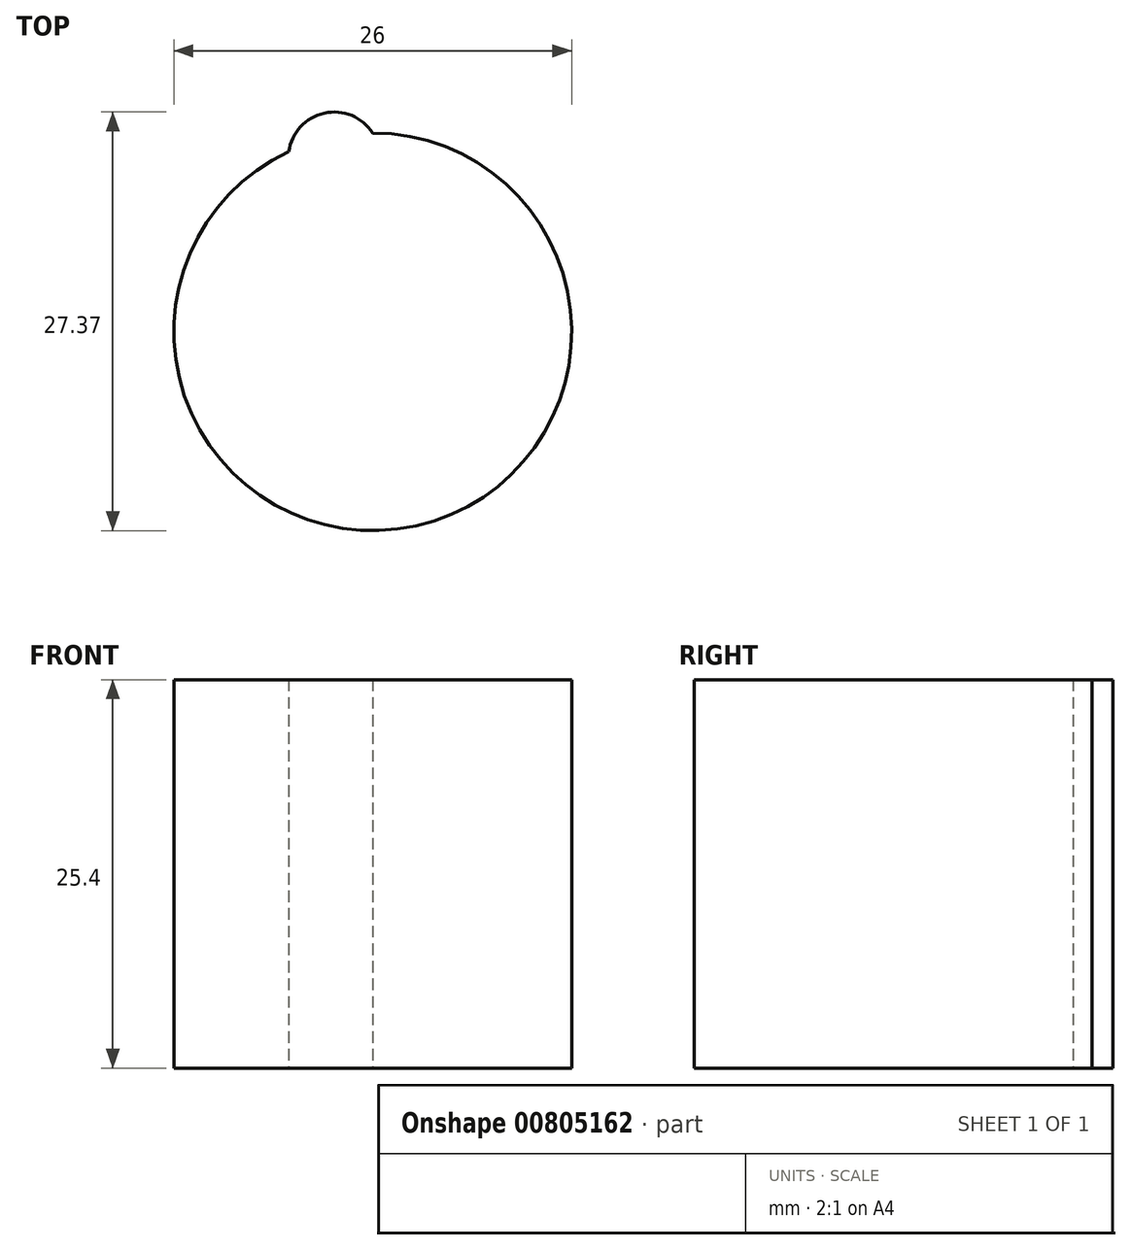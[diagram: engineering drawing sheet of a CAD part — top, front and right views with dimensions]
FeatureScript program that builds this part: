
annotation { "Feature Type Name" : "Feature", "Feature Type Description" : "" }
export const myFeature = defineFeature(function(context is Context, id is Id, definition is map)
    precondition{}
    {
        {
            var Q0;
            Q0=qCreatedBy(makeId("Top.planeOp"),FACE);
            var sketch = newSketch(context, id + "F0", { "sketchPlane" : qUnion([Q0])});
            skCircle(sketch, "E0", {"center": v(0, 0) * mm, "radius": 13 * mm});
            skArc(sketch, "E1", {"start": v(0, 13) * mm, "mid": v(-3.17, 14.3) * mm, "end": v(-5.5, 11.78) * mm});
            skArc(sketch, "E2.1.0", {"start": v(-5.66, 11.7) * mm, "mid": v(-9.08, 11.5) * mm, "end": v(-10.08, 8.22) * mm});
            skArc(sketch, "E2.2.0", {"start": v(-10.2, 8.07) * mm, "mid": v(-13.19, 6.4) * mm, "end": v(-12.67, 3.02) * mm});
            skArc(sketch, "E2.3.0", {"start": v(-12.7, 2.83) * mm, "mid": v(-14.68, 0.03) * mm, "end": v(-12.74, -2.8) * mm});
            skArc(sketch, "E2.4.0", {"start": v(-12.7, -2.98) * mm, "mid": v(-13.26, -6.36) * mm, "end": v(-10.3, -8.06) * mm});
            skArc(sketch, "E2.5.0", {"start": v(-10.17, -8.21) * mm, "mid": v(-9.2, -11.5) * mm, "end": v(-5.8, -11.74) * mm});
            skArc(sketch, "E2.6.0", {"start": v(-5.62, -11.82) * mm, "mid": v(-3.33, -14.37) * mm, "end": v(-0.15, -13.11) * mm});
            skArc(sketch, "E2.7.0", {"start": v(0.05, -13.1) * mm, "mid": v(3.21, -14.4) * mm, "end": v(5.54, -11.9) * mm});
            skArc(sketch, "E2.8.0", {"start": v(5.7, -11.8) * mm, "mid": v(9.13, -11.6) * mm, "end": v(10.13, -8.33) * mm});
            skArc(sketch, "E2.9.0", {"start": v(10.24, -8.17) * mm, "mid": v(13.23, -6.5) * mm, "end": v(12.72, -3.12) * mm});
            skArc(sketch, "E2.10.0", {"start": v(12.75, -2.94) * mm, "mid": v(14.73, -0.14) * mm, "end": v(12.8, 2.69) * mm});
            skArc(sketch, "E2.11.0", {"start": v(12.74, 2.87) * mm, "mid": v(13.3, 6.25) * mm, "end": v(10.34, 7.96) * mm});
            skPoint(sketch, "E2.center", {"position": v(0.02, -0.05) * mm});
            skArc(sketch, "E3.2.12.0", {"start": v(10.21, 8.1) * mm, "mid": v(9.26, 11.4) * mm, "end": v(5.84, 11.64) * mm});
            skArc(sketch, "E3.2.13.0", {"start": v(5.67, 11.72) * mm, "mid": v(3.38, 14.26) * mm, "end": v(0.2, 13) * mm});
            skSolve(sketch);
        }
        {
            var Q0;
            {var subQ0=sQuery(id+"F0.wireOp",EDGE,"E1");var subQ1=sQuery(id+"F0.wireOp",EDGE,"E0");var subQ2=makeQuery(id+"F0.imprint","INTERSECT",VERTEX,{"disambiguationData":[OD(0.0)],"derivedFrom":[subQ1,subQ0]});Q0=makeQuery(id+"F0.imprint","IMPRINT",FACE,{"disambiguationData":[TD([[makeQuery(id+"F0.imprint","IMPRINT",EDGE,{"disambiguationData":[TD([[subQ2,-1.0]])],"derivedFrom":subQ1}),1.0]])]});}
            var Q1;
            {var subQ0=sQuery(id+"F0.wireOp",EDGE,"E1");Q1=makeQuery(id+"F0.imprint","IMPRINT",FACE,{"disambiguationData":[TD([[makeQuery(id+"F0.imprint","IMPRINT",EDGE,{"derivedFrom":subQ0}),1.0]])]});}
            extrude(context, id + "F1", {"entities" : qUnion([Q0, Q1]), "depth" : 25.4 * mm, "offsetDistance" : 25.4 * mm});
        }
    });
